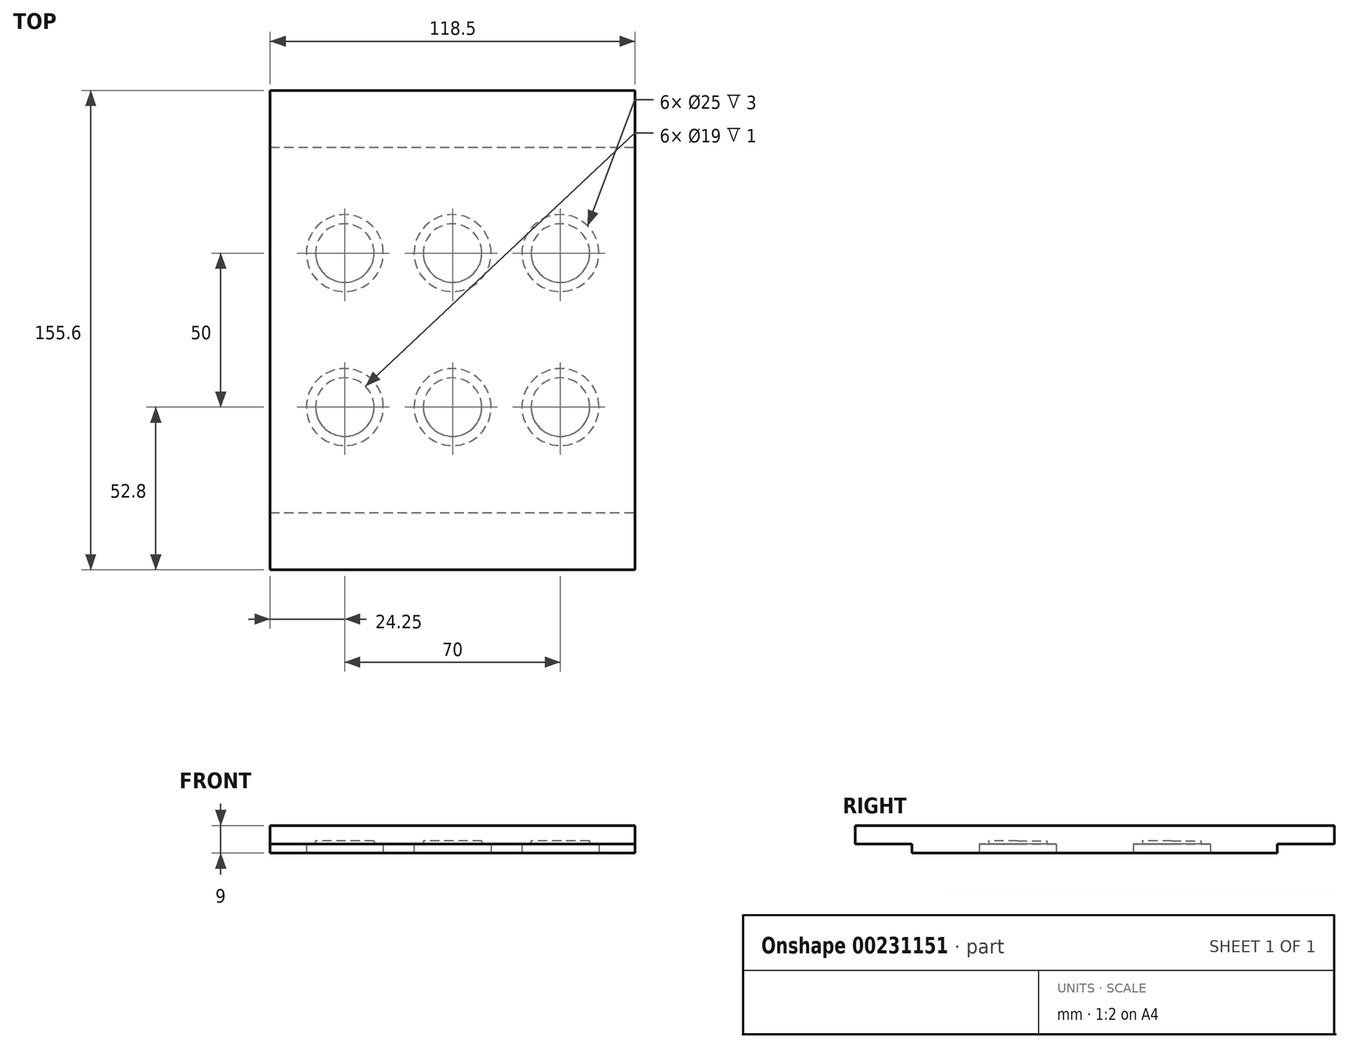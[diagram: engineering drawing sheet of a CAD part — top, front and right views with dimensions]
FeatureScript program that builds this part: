
annotation { "Feature Type Name" : "Feature", "Feature Type Description" : "" }
export const myFeature = defineFeature(function(context is Context, id is Id, definition is map)
    precondition{}
    {
        {
            var Q0;
            Q0=qCreatedBy(makeId("Top.planeOp"),FACE);
            var sketch = newSketch(context, id + "F0", { "sketchPlane" : qUnion([Q0])});
            skLineSegment(sketch, "E0.bottom", {"start": v(-59.25, 77.8) * mm, "end": v(59.25, 77.8) * mm});
            skLineSegment(sketch, "E0.top", {"start": v(-59.25, -77.8) * mm, "end": v(59.25, -77.8) * mm});
            skLineSegment(sketch, "E0.left", {"start": v(-59.25, 77.8) * mm, "end": v(-59.25, -77.8) * mm});
            skLineSegment(sketch, "E0.right", {"start": v(59.25, 77.8) * mm, "end": v(59.25, -77.8) * mm});
            skCircle(sketch, "E1", {"center": v(-35, 25) * mm, "radius": 9.5 * mm});
            skCircle(sketch, "E2.1.0.0", {"center": v(0, 25) * mm, "radius": 9.5 * mm});
            skCircle(sketch, "E2.2.0.0", {"center": v(35, 25) * mm, "radius": 9.5 * mm});
            skLineSegment(sketch, "E2.direction1", {"start": v(-35, 25) * mm, "end": v(0, 25) * mm, "construction": true});
            skCircle(sketch, "E3.0.1.0", {"center": v(-35, -25) * mm, "radius": 9.5 * mm});
            skCircle(sketch, "E3.1.1.0", {"center": v(0, -25) * mm, "radius": 9.5 * mm});
            skCircle(sketch, "E3.2.1.0", {"center": v(35, -25) * mm, "radius": 9.5 * mm});
            skLineSegment(sketch, "E3.direction2", {"start": v(-35, 25) * mm, "end": v(-35, -25) * mm, "construction": true});
            skSolve(sketch);
        }
        {
            var Q0;
            Q0=makeQuery(id+"F0.imprint","IMPRINT",FACE,{"disambiguationData":[TD([[makeQuery(id+"F0.imprint","IMPRINT",EDGE,{"derivedFrom":sQuery(id+"F0.wireOp",EDGE,"E0.bottom")}),-1.0]])]});
            extrude(context, id + "F1", {"entities" : qUnion([Q0]), "depth" : 4 * mm});
        }
        {
            var Q0;
            Q0=makeQuery(id+"F1.opExtrude","CAP_FACE",FACE,{"disambiguationData":[OSD([sQuery(id+"F0.wireOp",EDGE,"E0.bottom"),sQuery(id+"F0.wireOp",EDGE,"E0.top"),sQuery(id+"F0.wireOp",EDGE,"E0.left"),sQuery(id+"F0.wireOp",EDGE,"E0.right"),sQuery(id+"F0.wireOp",EDGE,"E1"),sQuery(id+"F0.wireOp",EDGE,"E3.0.1.0"),sQuery(id+"F0.wireOp",EDGE,"E2.1.0.0"),sQuery(id+"F0.wireOp",EDGE,"E3.1.1.0"),sQuery(id+"F0.wireOp",EDGE,"E2.2.0.0"),sQuery(id+"F0.wireOp",EDGE,"E3.2.1.0")])],"isStart":false});
            var sketch = newSketch(context, id + "F2", { "sketchPlane" : qUnion([Q0])});
            skLineSegment(sketch, "E4.bottom", {"start": v(-59.25, 77.8) * mm, "end": v(59.25, 77.8) * mm});
            skLineSegment(sketch, "E4.top", {"start": v(-59.25, -77.8) * mm, "end": v(59.25, -77.8) * mm});
            skLineSegment(sketch, "E4.left", {"start": v(-59.25, 77.8) * mm, "end": v(-59.25, -77.8) * mm});
            skLineSegment(sketch, "E4.right", {"start": v(59.25, 77.8) * mm, "end": v(59.25, -77.8) * mm});
            skSolve(sketch);
        }
        {
            var Q0;
            Q0 = qSketchRegion(id + "F2", true);
            extrude(context, id + "F3", {"entities" : qUnion([Q0]), "operationType" : NewBodyOperationType.ADD, "depth" : 5 * mm});
        }
        {
            var Q0;
            Q0=makeQuery(id+"F1.opExtrude","CAP_FACE",FACE,{"disambiguationData":[OSD([sQuery(id+"F0.wireOp",EDGE,"E0.bottom"),sQuery(id+"F0.wireOp",EDGE,"E0.top"),sQuery(id+"F0.wireOp",EDGE,"E0.left"),sQuery(id+"F0.wireOp",EDGE,"E0.right"),sQuery(id+"F0.wireOp",EDGE,"E1"),sQuery(id+"F0.wireOp",EDGE,"E3.0.1.0"),sQuery(id+"F0.wireOp",EDGE,"E2.1.0.0"),sQuery(id+"F0.wireOp",EDGE,"E3.1.1.0"),sQuery(id+"F0.wireOp",EDGE,"E2.2.0.0"),sQuery(id+"F0.wireOp",EDGE,"E3.2.1.0")])],"isStart":true});
            var sketch = newSketch(context, id + "F4", { "sketchPlane" : qUnion([Q0])});
            skCircle(sketch, "E5", {"center": v(-35, 25) * mm, "radius": 12.5 * mm});
            skCircle(sketch, "E6.0.1.0", {"center": v(-35, -25) * mm, "radius": 12.5 * mm});
            skCircle(sketch, "E6.1.0.0", {"center": v(0, 25) * mm, "radius": 12.5 * mm});
            skCircle(sketch, "E6.1.1.0", {"center": v(0, -25) * mm, "radius": 12.5 * mm});
            skCircle(sketch, "E6.2.0.0", {"center": v(35, 25) * mm, "radius": 12.5 * mm});
            skCircle(sketch, "E6.2.1.0", {"center": v(35, -25) * mm, "radius": 12.5 * mm});
            skLineSegment(sketch, "E6.direction1", {"start": v(-35, 25) * mm, "end": v(0, 25) * mm, "construction": true});
            skLineSegment(sketch, "E6.direction2", {"start": v(-35, 25) * mm, "end": v(-35, -25) * mm, "construction": true});
            skLineSegment(sketch, "E7.bottom", {"start": v(-59.25, 77.8) * mm, "end": v(59.25, 77.8) * mm});
            skLineSegment(sketch, "E7.top", {"start": v(-59.25, 59.3) * mm, "end": v(59.25, 59.3) * mm});
            skLineSegment(sketch, "E7.left", {"start": v(-59.25, 77.8) * mm, "end": v(-59.25, 59.3) * mm});
            skLineSegment(sketch, "E7.right", {"start": v(59.25, 77.8) * mm, "end": v(59.25, 59.3) * mm});
            skLineSegment(sketch, "E8.bottom", {"start": v(-59.25, -77.8) * mm, "end": v(59.25, -77.8) * mm});
            skLineSegment(sketch, "E8.top", {"start": v(-59.25, -59.3) * mm, "end": v(59.25, -59.3) * mm});
            skLineSegment(sketch, "E8.left", {"start": v(-59.25, -77.8) * mm, "end": v(-59.25, -59.3) * mm});
            skLineSegment(sketch, "E8.right", {"start": v(59.25, -77.8) * mm, "end": v(59.25, -59.3) * mm});
            skSolve(sketch);
        }
        {
            var Q0;
            Q0 = qSketchRegion(id + "F4", true);
            extrude(context, id + "F5", {"entities" : qUnion([Q0]), "operationType" : NewBodyOperationType.REMOVE, "oppositeDirection" : true, "depth" : 3 * mm});
        }
    });
